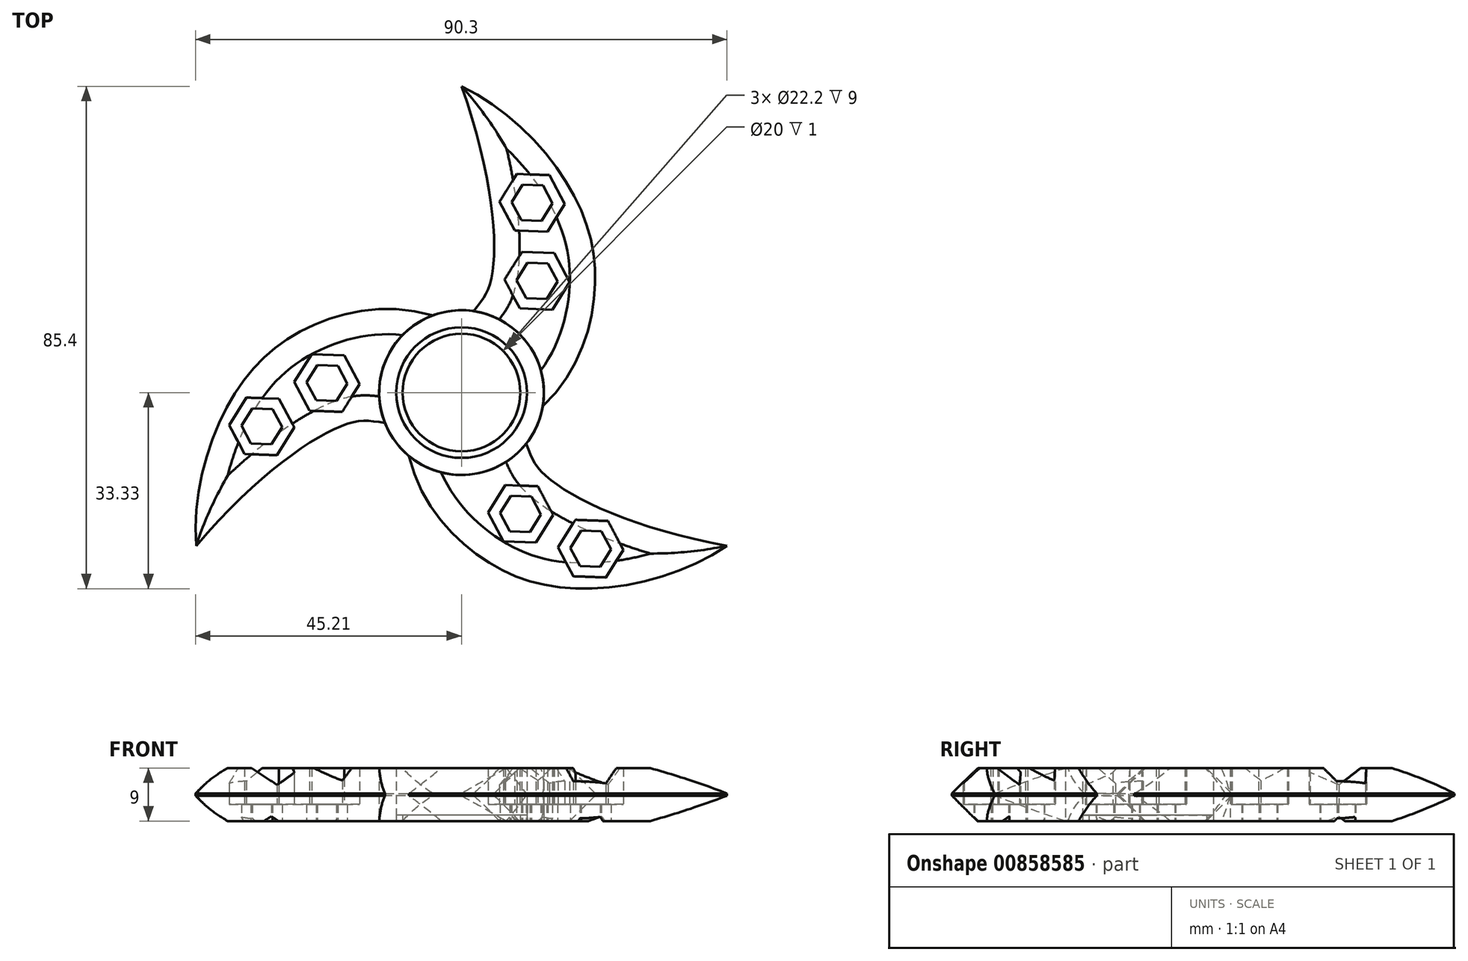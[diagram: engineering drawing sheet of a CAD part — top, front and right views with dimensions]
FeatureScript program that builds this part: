
annotation { "Feature Type Name" : "Feature", "Feature Type Description" : "" }
export const myFeature = defineFeature(function(context is Context, id is Id, definition is map)
    precondition{}
    {
        {
            var Q0;
            Q0=qCreatedBy(makeId("Top.planeOp"),FACE);
            var sketch = newSketch(context, id + "F0", { "sketchPlane" : qUnion([Q0])});
            skCircle(sketch, "E0", {"center": v(0, 0) * mm, "radius": 11.1 * mm});
            skLineSegment(sketch, "E1", {"start": v(0, 0) * mm, "end": v(0, 52.07) * mm, "construction": true});
            skLineSegment(sketch, "E2", {"start": v(0, 0) * mm, "end": v(63.41, -36.61) * mm, "construction": true});
            skFitSpline(sketch, "E3", {"points": [v(9.61, -5.55) * mm, v(22.5, 15.72) * mm, v(18.7, 34.28) * mm, v(0, 52.07) * mm], "startDerivative": vector(73.68, 46.4) * mm, "endDerivative": vector(-66.47, 31.25) * mm});
            skFitSpline(sketch, "E4", {"points": [v(0, 11.1) * mm, v(4.87, 18.55) * mm, v(0, 52.07) * mm], "startDerivative": vector(23.6, 34.07) * mm, "endDerivative": vector(-25.43, 71.66) * mm});
            skCircle(sketch, "E5", {"center": v(0, 0) * mm, "radius": 14 * mm});
            skCircle(sketch, "E6.cCircle", {"center": v(12, 32.27) * mm, "radius": 4.8 * mm, "construction": true});
            skLineSegment(sketch, "E6.0", {"start": v(17.54, 32.08) * mm, "end": v(14.6, 27.38) * mm});
            skLineSegment(sketch, "E6.1", {"start": v(14.6, 27.38) * mm, "end": v(9.06, 27.57) * mm});
            skLineSegment(sketch, "E6.2", {"start": v(9.06, 27.57) * mm, "end": v(6.46, 32.47) * mm});
            skLineSegment(sketch, "E6.3", {"start": v(6.46, 32.47) * mm, "end": v(9.4, 37.17) * mm});
            skLineSegment(sketch, "E6.4", {"start": v(9.4, 37.17) * mm, "end": v(14.94, 36.97) * mm});
            skLineSegment(sketch, "E6.5", {"start": v(14.94, 36.97) * mm, "end": v(17.54, 32.08) * mm});
            skPoint(sketch, "E6.0.midPoint", {"position": v(16.07, 29.73) * mm});
            skLineSegment(sketch, "E7.0.1.0", {"start": v(15.44, 14.1) * mm, "end": v(9.9, 14.3) * mm});
            skLineSegment(sketch, "E7.0.1.1", {"start": v(9.9, 14.3) * mm, "end": v(7.3, 19.2) * mm});
            skLineSegment(sketch, "E7.0.1.2", {"start": v(7.3, 19.2) * mm, "end": v(10.24, 23.9) * mm});
            skLineSegment(sketch, "E7.0.1.3", {"start": v(10.24, 23.9) * mm, "end": v(15.78, 23.7) * mm});
            skLineSegment(sketch, "E7.0.1.4", {"start": v(15.78, 23.7) * mm, "end": v(18.38, 18.8) * mm});
            skLineSegment(sketch, "E7.0.1.5", {"start": v(18.38, 18.8) * mm, "end": v(15.44, 14.1) * mm});
            skLineSegment(sketch, "E7.direction1", {"start": v(9.06, 27.57) * mm, "end": v(34.06, 27.57) * mm, "construction": true});
            skLineSegment(sketch, "E7.direction2", {"start": v(9.06, 27.57) * mm, "end": v(9.9, 14.3) * mm, "construction": true});
            skCircle(sketch, "E8", {"center": v(0, 0) * mm, "radius": 10 * mm});
            skCircle(sketch, "E9.cCircle", {"center": v(12, 32.27) * mm, "radius": 3 * mm, "construction": true});
            skLineSegment(sketch, "E9.0", {"start": v(15.46, 32.15) * mm, "end": v(13.62, 29.21) * mm});
            skLineSegment(sketch, "E9.1", {"start": v(13.62, 29.21) * mm, "end": v(10.16, 29.34) * mm});
            skLineSegment(sketch, "E9.2", {"start": v(10.16, 29.34) * mm, "end": v(8.54, 32.4) * mm});
            skLineSegment(sketch, "E9.3", {"start": v(8.54, 32.4) * mm, "end": v(10.37, 35.33) * mm});
            skLineSegment(sketch, "E9.4", {"start": v(10.37, 35.33) * mm, "end": v(13.84, 35.2) * mm});
            skLineSegment(sketch, "E9.5", {"start": v(13.84, 35.2) * mm, "end": v(15.46, 32.15) * mm});
            skPoint(sketch, "E9.0.midPoint", {"position": v(14.54, 30.68) * mm});
            skLineSegment(sketch, "E10", {"start": v(10.24, 23.9) * mm, "end": v(15.44, 14.1) * mm, "construction": true});
            skLineSegment(sketch, "E11", {"start": v(15.78, 23.7) * mm, "end": v(9.9, 14.3) * mm, "construction": true});
            skCircle(sketch, "E12.cCircle", {"center": v(12.84, 19) * mm, "radius": 3 * mm, "construction": true});
            skLineSegment(sketch, "E12.0", {"start": v(16.3, 18.88) * mm, "end": v(14.46, 15.94) * mm});
            skLineSegment(sketch, "E12.1", {"start": v(14.46, 15.94) * mm, "end": v(11, 16.06) * mm});
            skLineSegment(sketch, "E12.2", {"start": v(11, 16.06) * mm, "end": v(9.38, 19.12) * mm});
            skLineSegment(sketch, "E12.3", {"start": v(9.38, 19.12) * mm, "end": v(11.22, 22.06) * mm});
            skLineSegment(sketch, "E12.4", {"start": v(11.22, 22.06) * mm, "end": v(14.68, 21.94) * mm});
            skLineSegment(sketch, "E12.5", {"start": v(14.68, 21.94) * mm, "end": v(16.3, 18.88) * mm});
            skPoint(sketch, "E12.0.midPoint", {"position": v(15.38, 17.4) * mm});
            skSolve(sketch);
        }
        {
            var Q0;
            Q0=qSketchRegion(id+"F0",true);
            extrude(context, id + "F1", {"entities" : qUnion([Q0]), "depth" : 9 * mm, "offsetDistance" : 25 * mm});
        }
        {
            var Q0;
            {var subQ0=sQuery(id+"F0.wireOp",EDGE,"E0");var subQ1=makeQuery(id+"F0.imprint","INTERSECT",VERTEX,{"derivedFrom":[subQ0,sQuery(id+"F0.wireOp",EDGE,"E3")]});Q0=makeQuery(id+"F0.imprint","IMPRINT",FACE,{"disambiguationData":[TD([[makeQuery(id+"F0.imprint","IMPRINT",EDGE,{"disambiguationData":[TD([[subQ1,1.0]])],"derivedFrom":subQ0}),1.0]])]});}
            extrude(context, id + "F2", {"entities" : qUnion([Q0]), "depth" : 1 * mm, "offsetDistance" : 25 * mm});
        }
        {
            var Q0;
            Q0=makeQuery(id+"F0.imprint","IMPRINT",FACE,{"disambiguationData":[TD([[makeQuery(id+"F0.imprint","IMPRINT",EDGE,{"derivedFrom":sQuery(id+"F0.wireOp",EDGE,"E6.0")}),-1.0]])]});
            var Q1;
            Q1=makeQuery(id+"F0.imprint","IMPRINT",FACE,{"disambiguationData":[TD([[makeQuery(id+"F0.imprint","IMPRINT",EDGE,{"derivedFrom":sQuery(id+"F0.wireOp",EDGE,"E7.0.1.0")}),-1.0]])]});
            extrude(context, id + "F3", {"entities" : qUnion([Q0, Q1]), "operationType" : NewBodyOperationType.ADD, "depth" : 2.85 * mm, "offsetDistance" : 25 * mm});
        }
        {
            var Q0;
            Q0=qCreatedBy(makeId("Front.planeOp"),FACE);
            var sketch = newSketch(context, id + "F4", { "sketchPlane" : qUnion([Q0])});
            skLineSegment(sketch, "E13", {"start": v(0, 0) * mm, "end": v(0, 39.09) * mm, "construction": true});
            skSolve(sketch);
        }
        {
            var Q0;
            Q0=makeQuery(id+"F1.opExtrude","SWEPT_BODY",BODY,{"disambiguationData":[OSD([sQuery(id+"F0.wireOp",EDGE,"E0"),sQuery(id+"F0.wireOp",EDGE,"E3"),sQuery(id+"F0.wireOp",EDGE,"E4"),sQuery(id+"F0.wireOp",EDGE,"E5"),sQuery(id+"F0.wireOp",EDGE,"E6.0"),sQuery(id+"F0.wireOp",EDGE,"E6.1"),sQuery(id+"F0.wireOp",EDGE,"E6.2"),sQuery(id+"F0.wireOp",EDGE,"E6.3"),sQuery(id+"F0.wireOp",EDGE,"E6.4"),sQuery(id+"F0.wireOp",EDGE,"E6.5"),sQuery(id+"F0.wireOp",EDGE,"E7.0.1.0"),sQuery(id+"F0.wireOp",EDGE,"E7.0.1.1"),sQuery(id+"F0.wireOp",EDGE,"E7.0.1.2"),sQuery(id+"F0.wireOp",EDGE,"E7.0.1.3"),sQuery(id+"F0.wireOp",EDGE,"E7.0.1.4"),sQuery(id+"F0.wireOp",EDGE,"E7.0.1.5")])]});
            var Q1;
            Q1=sQuery(id+"F4.wireOp",EDGE,"E13");
            circularPattern(context, id + "F5", {"entities" : qUnion([Q0]), "axis" : qUnion([Q1]), "angle" : 360 * degree, "instanceCount" : 3, "equalSpace" : true});
        }
        {
            var Q0;
            Q0=makeQuery(id+"F5.opPattern","COPY",EDGE,{"derivedFrom":makeQuery(id+"F1.opExtrude","CAP_EDGE",EDGE,{"disambiguationData":[OSD([sQuery(id+"F0.wireOp",EDGE,"E4")])],"isStart":false}),"instanceName":"1"});
            var Q1;
            Q1=makeQuery(id+"F5.opPattern","COPY",EDGE,{"derivedFrom":makeQuery(id+"F1.opExtrude","CAP_EDGE",EDGE,{"disambiguationData":[OSD([sQuery(id+"F0.wireOp",EDGE,"E3")])],"isStart":false}),"instanceName":"1"});
            var Q2;
            Q2=makeQuery(id+"F5.opPattern","COPY",EDGE,{"derivedFrom":makeQuery(id+"F1.opExtrude","CAP_EDGE",EDGE,{"disambiguationData":[OSD([sQuery(id+"F0.wireOp",EDGE,"E4")])],"isStart":true}),"instanceName":"1"});
            var Q3;
            Q3=makeQuery(id+"F5.opPattern","COPY",EDGE,{"derivedFrom":makeQuery(id+"F1.opExtrude","CAP_EDGE",EDGE,{"disambiguationData":[OSD([sQuery(id+"F0.wireOp",EDGE,"E3")])],"isStart":true}),"instanceName":"1"});
            var Q4;
            Q4=makeQuery(id+"F5.opPattern","COPY",EDGE,{"derivedFrom":makeQuery(id+"F1.opExtrude","CAP_EDGE",EDGE,{"disambiguationData":[OSD([sQuery(id+"F0.wireOp",EDGE,"E3")])],"isStart":false}),"instanceName":"2"});
            var Q5;
            Q5=makeQuery(id+"F5.opPattern","COPY",EDGE,{"derivedFrom":makeQuery(id+"F1.opExtrude","CAP_EDGE",EDGE,{"disambiguationData":[OSD([sQuery(id+"F0.wireOp",EDGE,"E3")])],"isStart":true}),"instanceName":"2"});
            var Q6;
            Q6=makeQuery(id+"F5.opPattern","COPY",EDGE,{"derivedFrom":makeQuery(id+"F1.opExtrude","CAP_EDGE",EDGE,{"disambiguationData":[OSD([sQuery(id+"F0.wireOp",EDGE,"E4")])],"isStart":true}),"instanceName":"2"});
            var Q7;
            Q7=makeQuery(id+"F1.opExtrude","CAP_EDGE",EDGE,{"disambiguationData":[OSD([sQuery(id+"F0.wireOp",EDGE,"E3")])],"isStart":true});
            var Q8;
            Q8=makeQuery(id+"F1.opExtrude","CAP_EDGE",EDGE,{"disambiguationData":[OSD([sQuery(id+"F0.wireOp",EDGE,"E4")])],"isStart":true});
            var Q9;
            Q9=makeQuery(id+"F1.opExtrude","CAP_EDGE",EDGE,{"disambiguationData":[OSD([sQuery(id+"F0.wireOp",EDGE,"E3")])],"isStart":false});
            var Q10;
            Q10=makeQuery(id+"F1.opExtrude","CAP_EDGE",EDGE,{"disambiguationData":[OSD([sQuery(id+"F0.wireOp",EDGE,"E4")])],"isStart":false});
            var Q11;
            Q11=makeQuery(id+"F5.opPattern","COPY",EDGE,{"derivedFrom":makeQuery(id+"F1.opExtrude","CAP_EDGE",EDGE,{"disambiguationData":[OSD([sQuery(id+"F0.wireOp",EDGE,"E4")])],"isStart":false}),"instanceName":"2"});
            chamfer(context, id + "F6", {"entities" : qUnion([Q0, Q1, Q2, Q3, Q4, Q5, Q6, Q7, Q8, Q9, Q10, Q11]), "width" : 4.32 * mm, "tangentPropagation" : true});
        }
    });
